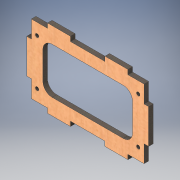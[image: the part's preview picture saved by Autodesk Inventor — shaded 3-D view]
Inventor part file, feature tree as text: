
AUTODESK INVENTOR PART (.ipt)
format: ipt  version: 2019 (Build 230136000, 136)  size: 177,664 bytes
history: native  units: mm
features: sketch x2, other x1, extrude x1, fillet x1, hole x1
ambient origin geometry x8: Origin, YZ Plane, XZ Plane, XY Plane, X Axis, Y Axis, Z Axis, Center Point
bodies: Body1 (feature_tree)
feature tree (6):
  other  "Твердое тело1"
  extrude  "Выдавливание1"  Depth=30.0mm
  fillet  "Сопряжение1"  Radius=4.0mm
  hole  "Отверстие1"  [1 undecoded]
  sketch  "Эскиз1"
  sketch  "Эскиз2"
note: 1 required parameter value undecoded (feature->parameter linkage not recoverable at this tier; creation-order binding heuristic only, values carry confidence <= 0.55)
